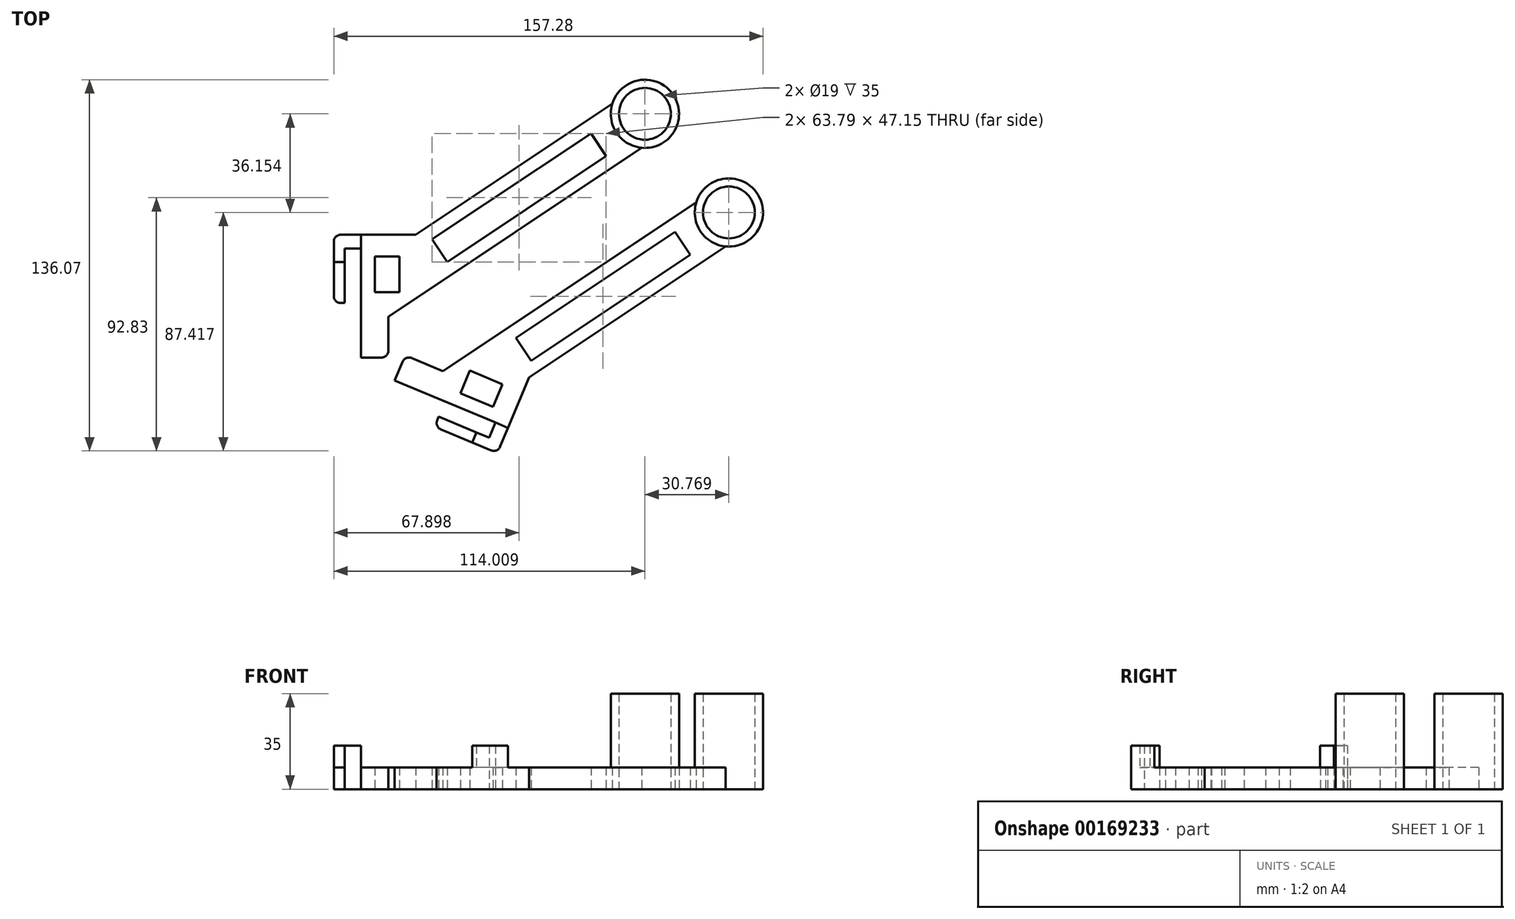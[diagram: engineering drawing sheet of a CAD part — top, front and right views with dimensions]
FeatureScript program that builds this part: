
annotation { "Feature Type Name" : "Feature", "Feature Type Description" : "" }
export const myFeature = defineFeature(function(context is Context, id is Id, definition is map)
    precondition{}
    {
        {
            var Q0;
            Q0=qCreatedBy(makeId("Top.planeOp"),FACE);
            var sketch = newSketch(context, id + "F0", { "sketchPlane" : qUnion([Q0])});
            skLineSegment(sketch, "E0", {"start": v(-44.07, 16.95) * mm, "end": v(-44.07, 36.95) * mm});
            skLineSegment(sketch, "E1", {"start": v(-44.07, 36.95) * mm, "end": v(-38.07, 36.95) * mm});
            skLineSegment(sketch, "E2", {"start": v(-38.07, 36.95) * mm, "end": v(-38.07, -3.05) * mm});
            skLineSegment(sketch, "E3", {"start": v(-38.07, -3.05) * mm, "end": v(-28.07, -3.05) * mm});
            skLineSegment(sketch, "E4", {"start": v(-28.07, -3.05) * mm, "end": v(-28.07, 11.95) * mm});
            skLineSegment(sketch, "E5", {"start": v(-28.07, 11.95) * mm, "end": v(64.77, 73.85) * mm});
            skLineSegment(sketch, "E6", {"start": v(54, 90) * mm, "end": v(-18.07, 41.95) * mm});
            skLineSegment(sketch, "E7", {"start": v(-18.07, 41.95) * mm, "end": v(-48.07, 41.95) * mm});
            skLineSegment(sketch, "E8", {"start": v(-48.07, 41.95) * mm, "end": v(-48.07, 16.95) * mm});
            skLineSegment(sketch, "E9", {"start": v(-48.07, 16.95) * mm, "end": v(-44.07, 16.95) * mm});
            skLineSegment(sketch, "E10.bottom", {"start": v(-33.07, 33.95) * mm, "end": v(-24.07, 33.95) * mm});
            skLineSegment(sketch, "E10.top", {"start": v(-33.07, 20.95) * mm, "end": v(-24.07, 20.95) * mm});
            skLineSegment(sketch, "E10.left", {"start": v(-33.07, 33.95) * mm, "end": v(-33.07, 20.95) * mm});
            skLineSegment(sketch, "E10.right", {"start": v(-24.07, 33.95) * mm, "end": v(-24.07, 20.95) * mm});
            skCircle(sketch, "E11", {"center": v(65.94, 86.3) * mm, "radius": 9.5 * mm});
            skLineSegment(sketch, "E12", {"start": v(65.94, 86.3) * mm, "end": v(-38.07, 16.95) * mm, "construction": true});
            skLineSegment(sketch, "E13", {"start": v(18.35, 42.9) * mm, "end": v(7.58, 59.05) * mm, "construction": true});
            skPoint(sketch, "E14", {"position": v(12.97, 50.98) * mm});
            skLineSegment(sketch, "E15", {"start": v(-12.07, 40.3) * mm, "end": v(-6.52, 31.98) * mm});
            skLineSegment(sketch, "E16", {"start": v(-6.52, 31.98) * mm, "end": v(51.72, 70.8) * mm});
            skLineSegment(sketch, "E17", {"start": v(51.72, 70.8) * mm, "end": v(46.18, 79.13) * mm});
            skLineSegment(sketch, "E18", {"start": v(46.18, 79.13) * mm, "end": v(-12.07, 40.3) * mm});
            skPoint(sketch, "E19", {"position": v(-9.3, 36.14) * mm});
            skCircle(sketch, "E20.0", {"center": v(65.94, 86.3) * mm, "radius": 12.5 * mm});
            skLineSegment(sketch, "E21", {"start": v(-48.07, 31.95) * mm, "end": v(-44.07, 31.95) * mm});
            skLineSegment(sketch, "E22", {"start": v(-38.07, 36.95) * mm, "end": v(-38.07, 41.95) * mm});
            skSolve(sketch);
        }
        {
            var Q0;
            Q0 = qSketchRegion(id + "F0", true);
            extrude(context, id + "F1", {"entities" : qUnion([Q0]), "depth" : 8 * mm});
        }
        {
            var Q0;
            Q0=makeQuery(id+"F0.imprint","IMPRINT",FACE,{"disambiguationData":[TD([[makeQuery(id+"F0.imprint","IMPRINT",EDGE,{"derivedFrom":sQuery(id+"F0.wireOp",EDGE,"E11")}),-1.0]])]});
            extrude(context, id + "F2", {"entities" : qUnion([Q0]), "operationType" : NewBodyOperationType.ADD, "depth" : 35 * mm});
        }
        {
            var Q0;
            {var subQ5=sQuery(id+"F0.wireOp",EDGE,"E1");Q0=makeQuery(id+"F0.imprint","IMPRINT",FACE,{"disambiguationData":[TD([[makeQuery(id+"F0.imprint","IMPRINT",EDGE,{"derivedFrom":subQ5}),1.0]])]});}
            extrude(context, id + "F3", {"entities" : qUnion([Q0]), "operationType" : NewBodyOperationType.ADD, "depth" : 16 * mm});
        }
        {
            var Q0;
            Q0=makeQuery(id+"F1.opExtrude","SWEPT_EDGE",EDGE,{"disambiguationData":[OSD([sQuery(id+"F0.wireOp",EDGE,"E3"),sQuery(id+"F0.wireOp",EDGE,"E4")])]});
            var Q1;
            Q1=makeQuery(id+"F1.opExtrude","SWEPT_EDGE",EDGE,{"disambiguationData":[OSD([sQuery(id+"F0.wireOp",EDGE,"E8"),sQuery(id+"F0.wireOp",EDGE,"E9")])]});
            var Q2;
            {var subQ0=sQuery(id+"F0.wireOp",EDGE,"E8");var subQ1=sQuery(id+"F0.wireOp",EDGE,"E7");Q2=makeQuery(id+"F3.boolean.opBoolean","MERGE",EDGE,{"derivedFrom":[makeQuery(id+"F1.opExtrude","SWEPT_EDGE",EDGE,{"disambiguationData":[OSD([subQ1,subQ0])]}),makeQuery(id+"F3.opExtrude","SWEPT_EDGE",EDGE,{"disambiguationData":[OSD([subQ1,subQ0])]})]});}
            fillet(context, id + "F4", {"entities" : qUnion([Q0, Q1, Q2]), "radius" : 2.5 * mm, "tangentPropagation" : true, "allowEdgeOverflow" : false});
        }
        {
            var Q0;
            Q0=makeQuery(id+"F1.opExtrude","SWEPT_BODY",BODY,{"disambiguationData":[OSD([sQuery(id+"F0.wireOp",EDGE,"E0"),sQuery(id+"F0.wireOp",EDGE,"E1"),sQuery(id+"F0.wireOp",EDGE,"E2"),sQuery(id+"F0.wireOp",EDGE,"E3"),sQuery(id+"F0.wireOp",EDGE,"E4"),sQuery(id+"F0.wireOp",EDGE,"E5"),sQuery(id+"F0.wireOp",EDGE,"E6"),sQuery(id+"F0.wireOp",EDGE,"E7"),sQuery(id+"F0.wireOp",EDGE,"E8"),sQuery(id+"F0.wireOp",EDGE,"E9"),sQuery(id+"F0.wireOp",EDGE,"E10.bottom"),sQuery(id+"F0.wireOp",EDGE,"E10.top"),sQuery(id+"F0.wireOp",EDGE,"E10.left"),sQuery(id+"F0.wireOp",EDGE,"E10.right"),sQuery(id+"F0.wireOp",EDGE,"E11"),sQuery(id+"F0.wireOp",EDGE,"E15"),sQuery(id+"F0.wireOp",EDGE,"E16"),sQuery(id+"F0.wireOp",EDGE,"E17"),sQuery(id+"F0.wireOp",EDGE,"E18"),sQuery(id+"F0.wireOp",EDGE,"E20.0")])]});
            var Q1;
            Q1=makeQuery(id+"F1.opExtrude","SWEPT_FACE",FACE,{"disambiguationData":[OSD([sQuery(id+"F0.wireOp",EDGE,"E5")])]});
            mirror(context, id + "F5", {"entities" : qUnion([Q0]), "mirrorPlane" : qUnion([Q1])});
        }
        {
            var Q0;
            Q0=makeQuery(id+"F5.opPattern","COPY",BODY,{"derivedFrom":makeQuery(id+"F1.opExtrude","SWEPT_BODY",BODY,{"disambiguationData":[OSD([sQuery(id+"F0.wireOp",EDGE,"E0"),sQuery(id+"F0.wireOp",EDGE,"E1"),sQuery(id+"F0.wireOp",EDGE,"E2"),sQuery(id+"F0.wireOp",EDGE,"E3"),sQuery(id+"F0.wireOp",EDGE,"E4"),sQuery(id+"F0.wireOp",EDGE,"E5"),sQuery(id+"F0.wireOp",EDGE,"E6"),sQuery(id+"F0.wireOp",EDGE,"E7"),sQuery(id+"F0.wireOp",EDGE,"E8"),sQuery(id+"F0.wireOp",EDGE,"E9"),sQuery(id+"F0.wireOp",EDGE,"E10.bottom"),sQuery(id+"F0.wireOp",EDGE,"E10.top"),sQuery(id+"F0.wireOp",EDGE,"E10.left"),sQuery(id+"F0.wireOp",EDGE,"E10.right"),sQuery(id+"F0.wireOp",EDGE,"E11"),sQuery(id+"F0.wireOp",EDGE,"E15"),sQuery(id+"F0.wireOp",EDGE,"E16"),sQuery(id+"F0.wireOp",EDGE,"E17"),sQuery(id+"F0.wireOp",EDGE,"E18"),sQuery(id+"F0.wireOp",EDGE,"E20.0")])]}),"instanceName":"1"});
            transform(context, id + "F6", {"entities" : qUnion([Q0]), "transformType" : TransformType.TRANSLATION_3D, "dx" : 20 * mm, "dy" : -20 * mm, "dz" : 0 * mm, "makeCopy" : false});
        }
    });
